# Revit family: Detector Térmico TDV-TDF ILUMAC
name_source: partatom
category: Dispositivos de alarme de incêndio
units: mm (PartAtom-declared; Revit-internal decimal feet)

## family parameters
Com base no plano de trabalho = Não
Compartilhado = Não
Corte com vazios quando carregada = Não
Cota do conector redondo = Utilizar diâmetro
Manter orientação da anotação = Não
Número OmniClass = 23.75.00.00
Ponto de cálculo do ambiente = Não
Sempre na vertical = Sim
Tipo de parte = Normal
Título OmniClass = Climate Control (HVAC)

## types (17) — shared parameters
Altura máxima e Área de cobertura = Até 5 metros de altura* e área de 36m2
Classe de aplicação = Classe A2
Fabricante = ILUMAC
Fixação = Base de sobrepor com terminais para a conexão dos cabos
Grau de proteção = IP20 (uso interno)
Material da caixa = Caixa plástica ABS na cor branco
Normas técnicas aplicáveis = NBR 17240 | ISO 7240-5
PLASTICO ABS = ABS BRANCO
Peso = 145g
Sensibilidade = 10mV / ºC
Tempo de inicialização = Até 15s
Tensão nominal = 24VCC
Umidade relativa = 0 à 85% (sem condensação)
zero-valued in all types: Elevação padrão

## per-type parameters (varying)
| type | Consumo | Código do produto | Descrição | Dimensões (AxLxP) | Endereços programáveis | Modelo | Modelo - Classe | Níveis de acionamento | Protocolo de comunicação | Temperatura de acionamento fixa | Temperatura de operação | Temperatura estática de reposta | Tempo de resposta | Tensão de operação | Termovelocimetria de acionamento | Tipo de detecção |
| TDV-C / Classe A2 | 110uA em supervisão / 30mA em alarme | 0010018 | Detector Térmico Convencional TDV-C / Classe A2 | ) 98mm de diâmetro e 45mm de profundidade (com a base) |  | TDV-C / Classe A2 | TDV-C |  |  | 57ºC | 5ºC à +50ºC | 54ºC à 70ºC | Até 300ms | 20 à 28VCC | >8ºC/min | TDV = Fixa e Termovelocimétrica TDF = Fixa |
| TDV-C / Classe B | 110uA em supervisão / 30mA em alarme | 0010019 | Detector Térmico Convencional TDV-C / Classe B | ) 98mm de diâmetro e 45mm de profundidade (com a base) |  | TDV-C / Classe B | TDV-C-B |  |  | 72ºC | -5ºC à +65ºC | 69ºC à 85ºC | Até 300ms | 20 à 28VCC | >10ºC/min | TDV = Fixa e Termovelocimétrica TDF = Fixa |
| TDF-C / Classe A2 | 110uA em supervisão / 30mA em alarme | 0010015 | Detector Térmico Convencional TDF-C / Classe A2 | ) 98mm de diâmetro e 45mm de profundidade (com a base) |  | TDF-C / Classe A2 | TDF-C / Classe A2 |  |  | 57ºC | -5ºC à +50ºC | 54ºC à 70ºC | Até 300ms | 20 à 28VCC |  | TDV = Fixa e Termovelocimétrica TDF = Fixa |
| TDF-C / Classe B | 110uA em supervisão / 30mA em alarme | 0010016 | Detector Térmico Convencional TDF-C / Classe B | ) 98mm de diâmetro e 45mm de profundidade (com a base) |  | TDF-C / Classe B | TDF-C / Classe A2 |  |  | 72ºC | -5ºC à +65ºC | 54ºC à 70ºC | Até 300ms | 20 à 28VCC |  | TDV = Fixa e Termovelocimétrica TDF = Fixa |
| TDV-E / Classe A2 | 340uA em supervisão / 1,3mA em alarme | 0020030 | Detector Térmico Endereçável TDV-E/ Classe A2 | 98mm de diâmetro e 45mm de profundidade (com a base) | 001 a 500 | TDV-E/ Classe A2 | TDV-E / Classe A2 |  | ALF-500 (proprietário) | 57ºC | -5ºC à +50ºC | 54ºC à 70ºC | Até 300ms | 22 à 28VCC | >8ºC/min | TDV = Fixa e Termovelocimétrica |
| TDV-E / Classe B | 340uA em supervisão / 1,3mA em alarme | 0020031 | Detector Térmico Endereçável TDV-E/ Classe B | 98mm de diâmetro e 45mm de profundidade (com a base) | 001 a 500 | TDV-E/ Classe B | TDV-E / Classe B |  | ALF-500 (proprietário) | 57ºC | -5ºC à +50ºC | 54ºC à 70ºC | Até 300ms | 22 à 28VCC |  | TDF = Fixa |
| TDF-E / Classe A2 | 340uA em supervisão / 1,3mA em alarme | 0020034 | Detector Térmico Endereçável TDF-E/ Classe A2 | 98mm de diâmetro e 45mm de profundidade (com a base) | 001 a 500 | TDF-E/ Classe A2 | TDF-E / Classe A2 |  | ALF-500 (proprietário) | 72ºC | -5ºC à +65ºC | 69ºC à 85ºC | Até 300ms | 22 à 28VCC | >10ºC/min | TDV = Fixa e Termovelocimétrica |
| TDF-E / Classe B | 340uA em supervisão / 1,3mA em alarme | 0020035 | Detector Térmico Endereçável TDF-E/ Classe B | 98mm de diâmetro e 45mm de profundidade (com a base) | 001 a 500 | TDF-E / Classe B | TDF-E / Classe B |  | ALF-500 (proprietário) | 72ºC | -5ºC à +65ºC | 69ºC à 85ºC | Até 300ms | 22 à 28VCC |  | TDF = Fixa |
| TDV-D / Classe A2 | o 800uA em supervisão / 1,7mA em alarme | 0040022 | Detector Térmico Endereçável Sirius TDV-D/ Classe A2 | 98mm de diâmetro e 45mm de profundidade (com a base) | 001 a 125 (por laço) | TDV-D/ Classe A2 | TDV-D / Classe A2 |  | ALF-1000-2 (proprietário) | 57ºC | -5ºC à +50ºC | 54ºC à 70ºC | Até 300ms | 20 à 30VCC | >8ºC/min | TDV = Fixa e Termovelocimétrica |
| TDV-D / Classe B | o 800uA em supervisão / 1,7mA em alarme | 0040023 | Detector Térmico Endereçável Sirius TDV-D/ Classe B | 98mm de diâmetro e 45mm de profundidade (com a base) | 001 a 125 (por laço) | TDV-D / Classe B | TDV-D / Classe B |  | ALF-1000-2 (proprietário) | 72ºC | -5ºC à +65ºC | 69ºC à 85ºC | Até 300ms | 20 à 30VCC | >10ºC/min | TDV = Fixa e Termovelocimétrica |
| TDF-D / Classe A2 | o 800uA em supervisão / 1,7mA em alarme | 0040024 | Detector Térmico Endereçável Sirius TDF-D/ Classe A2 | 98mm de diâmetro e 45mm de profundidade (com a base) | 001 a 125 (por laço) | TDF-D/ Classe A2 | TDV-D / Classe A2 |  | ALF-1000-2 (proprietário) | 57ºC | -5ºC à +50ºC | 54ºC à 70ºC | Até 300ms | 20 à 30VCC |  | TDF = Fixa |
| TDF-D / Classe B | o 800uA em supervisão / 1,7mA em alarme | 0040025 | Detector Térmico Endereçável Sirius TDF-D/ Classe B | 98mm de diâmetro e 45mm de profundidade (com a base) | 001 a 125 (por laço) | TDF-D / Classe B | TDV-D / Classe A2 |  | ALF-1000-2 (proprietário) | 72ºC | -5ºC à +65ºC | 69ºC à 85ºC | Até 300ms | 20 à 30VCC |  | TDF = Fixa |
| TDF-A | 800uA em supervisão
1,7mA em alarme | 0040051 | Detector Térmico Analógico Sirius TDF-A | 98mm de diâmetro e 45mm de profundidade (com a base) | 001 a 125 (por laço) | TDF-A | TDV-D / Classe A2 | 3 níveis: Baixo / Padrão / Alto
Ajustados pelo menu da central | ALF-1000-2 (proprietário) | Temperatura de acionamento no nível Sensibilidade Baixo: 69ºC
Temperatura de acionamento no nível Sensibilidade Padrão: 57ºC
Temperatura de acionamento no nível Sensibilidade Alto: 54ºC | -5ºC à +65ºC | 54ºC à 85ºC | Até 300 milissegundos | 24VCC / 20 à 30VCC |  | Fixa |
| TDV-G / Classe A2 | 900uA em supervisão / 2mA em alarme | 007040 | Detector Térmico Endereçável Cygnus TDV-G / Classe A2 | 98mm de diâmetro e 45mm de profundidade (com a base) | 001 a 125 (por laço) | TDV-G / Classe A2 | TDV-D / Classe A2 | 3 níveis: Baixo / Padrão / Alto
Ajustados pelo menu da central | CYGNUS (proprietário) | 57ºC
Temperatura de acionamento no nível Sensibilidade Padrão: 57ºC
Temperatura de acionamento no nível Sensibilidade Alto: 54ºC | -5ºC à +50ºC | 54ºC à 70ºC | Até 300 milissegundos | 20 à 30VCC | >8ºC/min | TDV = Fixa e Termovelocimét |
| TDV-G / Classe B | 900uA em supervisão / 2mA em alarme | 007041 | Detector Térmico Endereçável Cygnus TDV-G / Classe B | 98mm de diâmetro e 45mm de profundidade (com a base) | 001 a 125 (por laço) | TDV-G / Classe B | TDV-D / Classe A2 | 3 níveis: Baixo / Padrão / Alto
Ajustados pelo menu da central | CYGNUS (proprietário) | 57ºC
Temperatura de acionamento no nível Sensibilidade Padrão: 57ºC
Temperatura de acionamento no nível Sensibilidade Alto: 54ºC | -5ºC à +50ºC | 54ºC à 70ºC | Até 300 milissegundos | 20 à 30VCC |  | TDF = Fixa |
| TDF-G / Classe A2 | 900uA em supervisão / 2mA em alarme | 007042 | Detector Térmico Endereçável Cygnus TDF-G / Classe A2 | 98mm de diâmetro e 45mm de profundidade (com a base) | 001 a 125 (por laço) | TDF-G / Classe A2 | TDV-D / Classe A2 | 3 níveis: Baixo / Padrão / Alto
Ajustados pelo menu da central | CYGNUS (proprietário) | 72ºC | -5ºC à +65ºC | 69ºC à 85ºC | Até 300 milissegundos | 20 à 30VCC | >10ºC/min | TDV = Fixa e Termovelocimétrica |
| TDF-G / Classe B | 900uA em supervisão / 2mA em alarme | 007043 | Detector Térmico Endereçável Cygnus TDF-G / Classe B | 98mm de diâmetro e 45mm de profundidade (com a base) | 001 a 125 (por laço) | TDF-G / Classe B | TDV-D / Classe A2 | 3 níveis: Baixo / Padrão / Alto
Ajustados pelo menu da central | CYGNUS (proprietário) | 72ºC | -5ºC à +65ºC | 69ºC à 85ºC | Até 300 milissegundos | 20 à 30VCC |  | TDF = Fixa |
